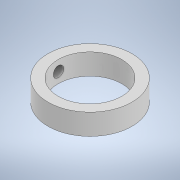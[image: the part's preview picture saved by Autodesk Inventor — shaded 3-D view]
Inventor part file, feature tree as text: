
AUTODESK INVENTOR PART (.ipt)
format: ipt  version: 2021 (Build 250183000, 183)  size: 112,640 bytes
history: native  units: mm
features: extrude x2, sketch x2
ambient origin geometry x8: Origin, YZ Plane, XZ Plane, XY Plane, X Axis, Y Axis, Z Axis, Center Point
bodies: Solid1 (feature_tree)
feature tree (4):
  extrude  "Extrusion1"  Depth=24.0mm
  extrude  "Extrusion2"  Depth=3.0mm
  sketch  "Sketch1"  dims[d0=18.2mm d1=24.0mm]
  sketch  "Sketch2"  dims[d2=6.0mm d3=0.0mm d4=3.0mm d5=3.0mm d6=0.0mm d7=0.0mm]
